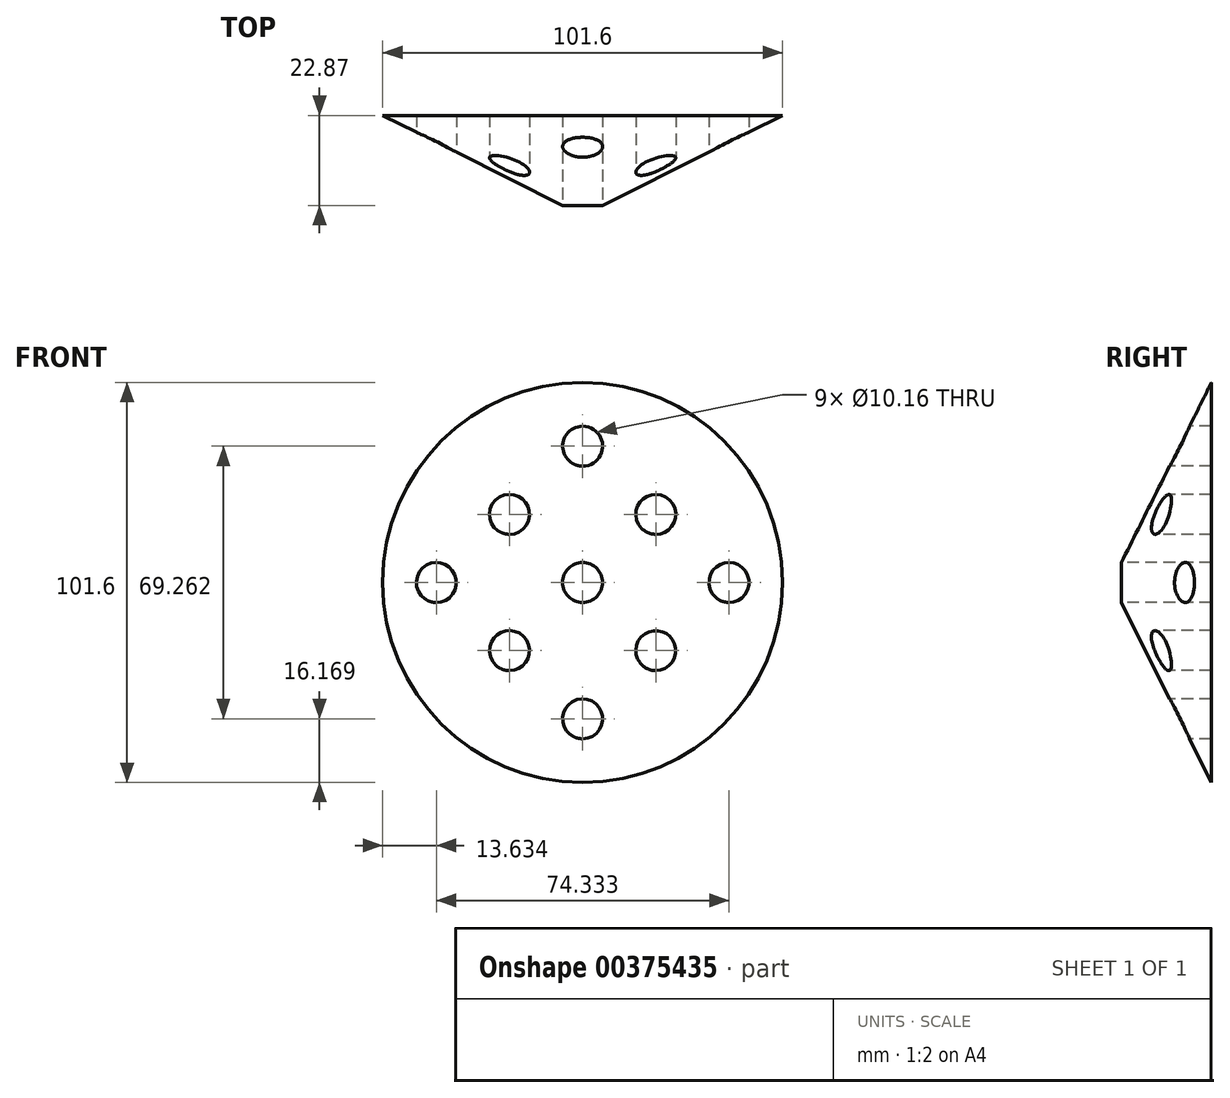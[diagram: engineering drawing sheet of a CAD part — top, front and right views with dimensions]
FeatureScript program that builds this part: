
annotation { "Feature Type Name" : "Feature", "Feature Type Description" : "" }
export const myFeature = defineFeature(function(context is Context, id is Id, definition is map)
    precondition{}
    {
        {
            var Q0;
            Q0=qCreatedBy(makeId("Front.planeOp"),FACE);
            var sketch = newSketch(context, id + "F0", { "sketchPlane" : qUnion([Q0])});
            skCircle(sketch, "E0", {"center": v(0, 0) * mm, "radius": 50.8 * mm});
            skSolve(sketch);
        }
        {
            var Q0;
            Q0 = qSketchRegion(id + "F0", true);
            extrude(context, id + "F1", {"entities" : qUnion([Q0]), "depth" : 25.4 * mm});
        }
        {
            var Q0;
            Q0=qCreatedBy(makeId("Right.planeOp"),FACE);
            var sketch = newSketch(context, id + "F2", { "sketchPlane" : qUnion([Q0])});
            skLineSegment(sketch, "E1", {"start": v(0, 0) * mm, "end": v(-43.66, 0) * mm});
            skSolve(sketch);
        }
        {
            var Q0;
            Q0=qCreatedBy(makeId("Top.planeOp"),FACE);
            var sketch = newSketch(context, id + "F3", { "sketchPlane" : qUnion([Q0])});
            skLineSegment(sketch, "E2", {"start": v(0, -25.4) * mm, "end": v(-50.82, -25.4) * mm});
            skLineSegment(sketch, "E3", {"start": v(-50.82, -25.4) * mm, "end": v(-50.82, 0) * mm});
            skLineSegment(sketch, "E4", {"start": v(-50.82, 0) * mm, "end": v(0, -25.4) * mm});
            skSolve(sketch);
        }
        {
            var Q0;
            Q0=makeQuery(id+"F3.imprint","IMPRINT",FACE,{"disambiguationData":[TD([[makeQuery(id+"F3.imprint","IMPRINT",EDGE,{"derivedFrom":sQuery(id+"F3.wireOp",EDGE,"E2")}),-1.0]])]});
            var Q1;
            Q1=sQuery(id+"F2.wireOp",EDGE,"E1");
            revolve(context, id + "F4", {"operationType" : NewBodyOperationType.REMOVE, "entities" : qUnion([Q0]), "axis" : qUnion([Q1]), "revolveType" : RevolveType.ONE_DIRECTION, "angle" : 350 * degree});
        }
        {
            var Q0;
            Q0=makeQuery(id+"F4.boolean.opBoolean","COPY",FACE,{"derivedFrom":makeQuery(id+"F4.opRevolve","CAP_FACE",FACE,{"disambiguationData":[OSD([sQuery(id+"F3.wireOp",EDGE,"E2"),sQuery(id+"F3.wireOp",EDGE,"E3"),sQuery(id+"F3.wireOp",EDGE,"E4")])],"isStart":false})});
            var Q1;
            Q1=sQuery(id+"F2.wireOp",EDGE,"E1");
            revolve(context, id + "F5", {"operationType" : NewBodyOperationType.REMOVE, "entities" : qUnion([Q0]), "axis" : qUnion([Q1]), "revolveType" : RevolveType.ONE_DIRECTION, "angle" : 25 * degree});
        }
        {
            var Q0;
            Q0=qCreatedBy(makeId("Front.planeOp"),FACE);
            cPlane(context, id + "F6", {"entities" : qUnion([Q0]), "cplaneType" : CPlaneType.OFFSET, "offset" : 25.4 * mm, "width" : 152.4 * mm, "height" : 152.4 * mm});
        }
        {
            var Q0;
            Q0=qCreatedBy(id+"F6.planeOp",FACE);
            var sketch = newSketch(context, id + "F7", { "sketchPlane" : qUnion([Q0])});
            skLineSegment(sketch, "E5.bottom", {"start": v(37.17, 34.63) * mm, "end": v(-37.17, 34.63) * mm, "construction": true});
            skLineSegment(sketch, "E5.top", {"start": v(37.17, -34.63) * mm, "end": v(-37.17, -34.63) * mm, "construction": true});
            skLineSegment(sketch, "E5.left", {"start": v(37.17, 34.63) * mm, "end": v(37.17, -34.63) * mm, "construction": true});
            skLineSegment(sketch, "E5.right", {"start": v(-37.17, 34.63) * mm, "end": v(-37.17, -34.63) * mm, "construction": true});
            skPoint(sketch, "E5.middle", {"position": v(0, 0) * mm});
            skCircle(sketch, "E6", {"center": v(0, -34.63) * mm, "radius": 5.08 * mm});
            skCircle(sketch, "E7", {"center": v(0, 34.63) * mm, "radius": 5.08 * mm});
            skCircle(sketch, "E8", {"center": v(-37.17, 0) * mm, "radius": 5.08 * mm});
            skCircle(sketch, "E9", {"center": v(37.17, 0) * mm, "radius": 5.08 * mm});
            skCircle(sketch, "E10", {"center": v(0, 0) * mm, "radius": 5.08 * mm});
            skLineSegment(sketch, "E11", {"start": v(-37.17, -34.63) * mm, "end": v(0, 0) * mm, "construction": true});
            skLineSegment(sketch, "E12", {"start": v(0, 0) * mm, "end": v(-37.17, 34.63) * mm, "construction": true});
            skLineSegment(sketch, "E13", {"start": v(0, 0) * mm, "end": v(37.17, -34.63) * mm, "construction": true});
            skLineSegment(sketch, "E14", {"start": v(0, 0) * mm, "end": v(37.17, 34.63) * mm, "construction": true});
            skLineSegment(sketch, "E15", {"start": v(0, 34.63) * mm, "end": v(37.17, 0) * mm, "construction": true});
            skLineSegment(sketch, "E16", {"start": v(0, -34.63) * mm, "end": v(37.17, 0) * mm, "construction": true});
            skLineSegment(sketch, "E17", {"start": v(0, -34.63) * mm, "end": v(-37.17, 0) * mm, "construction": true});
            skLineSegment(sketch, "E18", {"start": v(-37.17, 0) * mm, "end": v(0, 34.63) * mm, "construction": true});
            skCircle(sketch, "E19", {"center": v(-18.58, -17.32) * mm, "radius": 5.08 * mm});
            skCircle(sketch, "E20", {"center": v(-18.58, 17.32) * mm, "radius": 5.08 * mm});
            skCircle(sketch, "E21", {"center": v(18.58, 17.32) * mm, "radius": 5.08 * mm});
            skCircle(sketch, "E22", {"center": v(18.58, -17.32) * mm, "radius": 5.08 * mm});
            skSolve(sketch);
        }
        {
            var Q0;
            Q0 = qSketchRegion(id + "F7", true);
            extrude(context, id + "F8", {"entities" : qUnion([Q0]), "operationType" : NewBodyOperationType.REMOVE, "endBound" : BoundingType.THROUGH_ALL, "oppositeDirection" : true, "depth" : 25.4 * mm});
        }
    });
